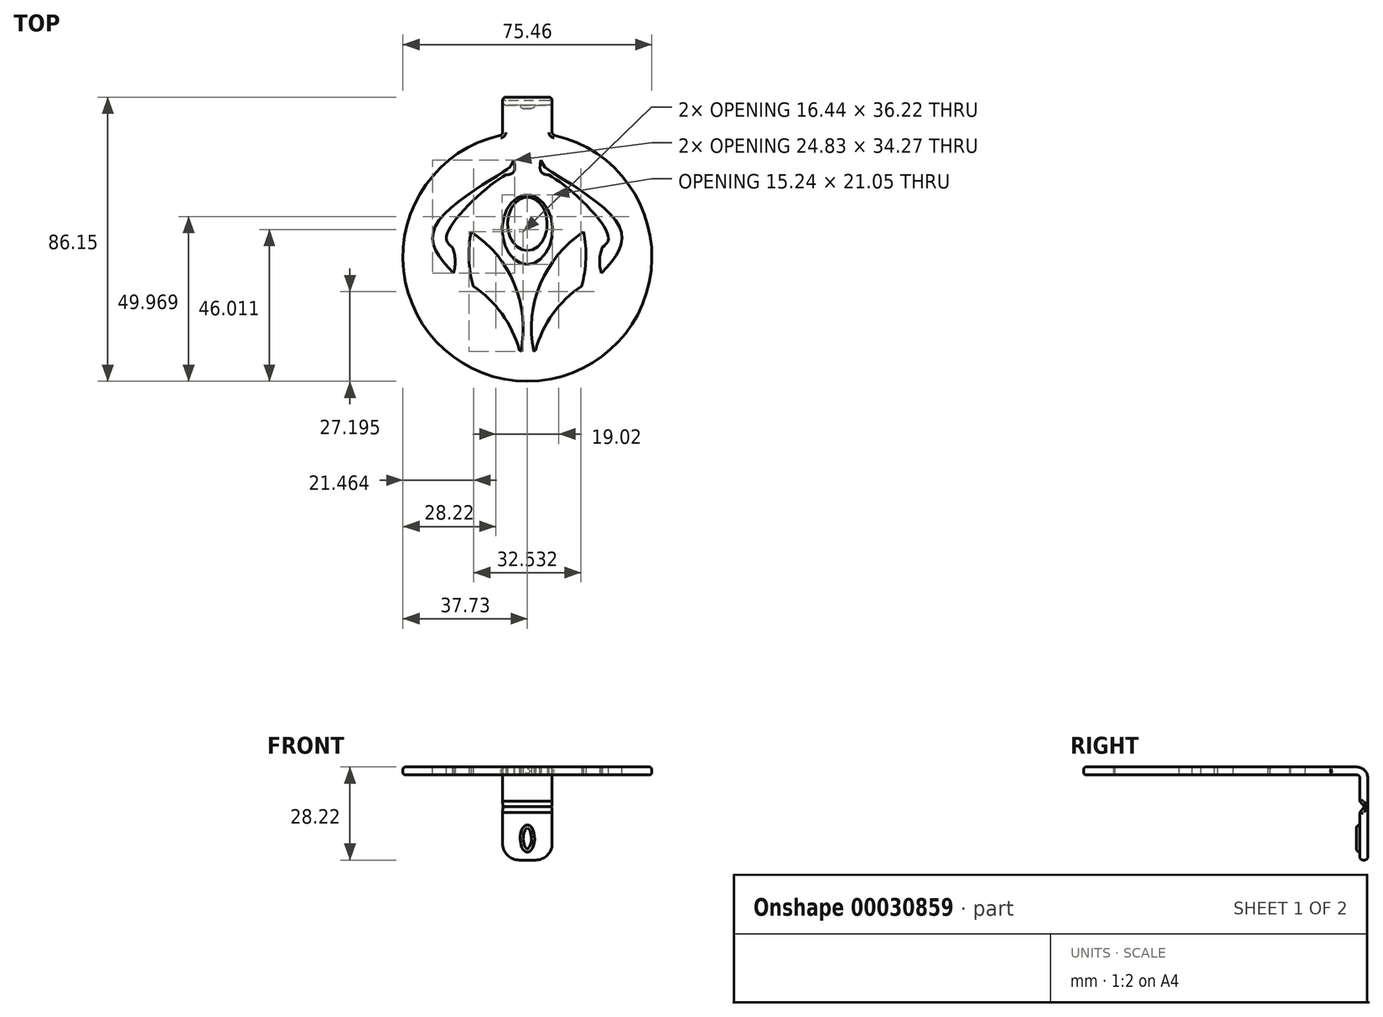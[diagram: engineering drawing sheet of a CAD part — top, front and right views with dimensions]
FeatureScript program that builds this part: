
annotation { "Feature Type Name" : "Feature", "Feature Type Description" : "" }
export const myFeature = defineFeature(function(context is Context, id is Id, definition is map)
    precondition{}
    {
        {
            var Q0;
            Q0=qCreatedBy(makeId("Top.planeOp"),FACE);
            var sketch = newSketch(context, id + "F0", { "sketchPlane" : qUnion([Q0])});
            skLineSegment(sketch, "E0", {"start": v(-75.5, -12.71) * mm, "end": v(-9.56, -74.3) * mm, "construction": true});
            skLineSegment(sketch, "E1", {"start": v(-4.86, -71.61) * mm, "end": v(-42.6, 18.94) * mm, "construction": true});
            skArc(sketch, "E2", {"start": v(-75.5, -12.71) * mm, "mid": v(-51.74, -53.37) * mm, "end": v(-9.56, -74.3) * mm});
            skArc(sketch, "E3", {"start": v(-4.86, -71.61) * mm, "mid": v(-9.83, -20.55) * mm, "end": v(-42.6, 18.94) * mm});
            skArc(sketch, "E4.MirrorCS", {"start": v(-75.5, -12.71) * mm, "mid": v(-33.32, -33.65) * mm, "end": v(-9.56, -74.3) * mm});
            skArc(sketch, "E5.0", {"start": v(-41.12, -22.06) * mm, "mid": v(-19.25, -43.28) * mm, "end": v(-6.12, -70.78) * mm});
            skArc(sketch, "E6.MirrorCS", {"start": v(-4.86, -71.61) * mm, "mid": v(-5.5, -71.2) * mm, "end": v(-6.12, -70.78) * mm});
            skArc(sketch, "E7.trimOffspring", {"start": v(-41.12, -22.06) * mm, "mid": v(-44.3, -1.65) * mm, "end": v(-42.6, 18.94) * mm});
            skArc(sketch, "E8.MirrorCS", {"start": v(75.5, -12.71) * mm, "mid": v(51.74, -53.37) * mm, "end": v(9.56, -74.3) * mm});
            skArc(sketch, "E9.MirrorCS", {"start": v(75.5, -12.71) * mm, "mid": v(33.32, -33.65) * mm, "end": v(9.56, -74.3) * mm});
            skArc(sketch, "E10.MirrorCS", {"start": v(41.12, -22.06) * mm, "mid": v(44.3, -1.65) * mm, "end": v(42.6, 18.94) * mm});
            skArc(sketch, "E11.MirrorCS", {"start": v(41.12, -22.06) * mm, "mid": v(19.25, -43.28) * mm, "end": v(6.12, -70.78) * mm});
            skArc(sketch, "E12.MirrorCS", {"start": v(4.86, -71.61) * mm, "mid": v(9.83, -20.55) * mm, "end": v(42.6, 18.94) * mm});
            skArc(sketch, "E13.MirrorCS", {"start": v(4.86, -71.61) * mm, "mid": v(5.5, -71.2) * mm, "end": v(6.12, -70.78) * mm});
            skSolve(sketch);
        }
        {
            var Q0;
            Q0=qCreatedBy(makeId("Top.planeOp"),FACE);
            var sketch = newSketch(context, id + "F1", { "sketchPlane" : qUnion([Q0])});
            skEllipse(sketch, "E14", {"center": v(0, 20.7) * mm, "majorRadius": 26.3 * mm, "minorRadius": 19.05 * mm, "majorAxis": v(0, -1)});
            skEllipse(sketch, "E15", {"center": v(0, 25) * mm, "majorRadius": 20.32 * mm, "minorRadius": 15 * mm, "majorAxis": v(0, -1)});
            skSolve(sketch);
        }
        {
            var Q0;
            Q0=qCreatedBy(makeId("Top.planeOp"),FACE);
            var sketch = newSketch(context, id + "F2", { "sketchPlane" : qUnion([Q0])});
            skFitSpline(sketch, "E16", {"points": [v(-10.32, 73.44) * mm, v(-14.62, 66.99) * mm, v(-69.19, 24.14) * mm, v(-56, -12.24) * mm], "startDerivative": vector(-33.58, -68.78) * mm, "endDerivative": vector(100.58, -102.34) * mm});
            skArc(sketch, "E17", {"start": v(-56, -12.24) * mm, "mid": v(-54.75, -2.43) * mm, "end": v(-56.87, 7.24) * mm});
            skFitSpline(sketch, "E18", {"points": [v(-56.87, 7.24) * mm, v(-60.9, 17.24) * mm, v(-16.13, 62.2) * mm], "startDerivative": vector(-32.39, 22.42) * mm, "endDerivative": vector(56.1, 28.88) * mm});
            skFitSpline(sketch, "E19", {"points": [v(-10.32, 73.44) * mm, v(-10.32, 64.63) * mm, v(-16.13, 62.2) * mm], "startDerivative": vector(3.32, -19.88) * mm, "endDerivative": vector(-13.95, 1.21) * mm});
            skFitSpline(sketch, "E20.MirrorCS", {"points": [v(10.32, 73.44) * mm, v(10.32, 64.63) * mm, v(16.13, 62.2) * mm], "startDerivative": vector(-3.32, -19.88) * mm, "endDerivative": vector(13.95, 1.21) * mm});
            skFitSpline(sketch, "E21.MirrorCS", {"points": [v(10.32, 73.44) * mm, v(14.62, 66.99) * mm, v(69.19, 24.14) * mm, v(56, -12.24) * mm], "startDerivative": vector(33.58, -68.78) * mm, "endDerivative": vector(-100.58, -102.34) * mm});
            skFitSpline(sketch, "E22.MirrorCS", {"points": [v(56.87, 7.24) * mm, v(60.9, 17.24) * mm, v(16.13, 62.2) * mm], "startDerivative": vector(32.39, 22.42) * mm, "endDerivative": vector(-56.1, 28.88) * mm});
            skArc(sketch, "E23.MirrorCS", {"start": v(56, -12.24) * mm, "mid": v(54.75, -2.43) * mm, "end": v(56.87, 7.24) * mm});
            skSolve(sketch);
        }
        {
            var Q0;
            Q0=qCreatedBy(makeId("Top.planeOp"),FACE);
            var sketch = newSketch(context, id + "F3", { "sketchPlane" : qUnion([Q0])});
            skCircle(sketch, "E24", {"center": v(0, 0) * mm, "radius": 94.33 * mm});
            skSolve(sketch);
        }
        {
            var Q0;
            Q0=makeQuery(id+"F3.imprint","IMPRINT",FACE,{"disambiguationData":[TD([[makeQuery(id+"F3.imprint","IMPRINT",EDGE,{"derivedFrom":sQuery(id+"F3.wireOp",EDGE,"E24")}),1.0]])]});
            extrude(context, id + "F4", {"entities" : qUnion([Q0]), "endBound" : BoundingType.SYMMETRIC, "depth" : 6 * mm});
        }
        {
            var Q0;
            Q0=makeQuery(id+"F0.imprint","IMPRINT",FACE,{"disambiguationData":[TD([[makeQuery(id+"F0.imprint","IMPRINT",EDGE,{"derivedFrom":sQuery(id+"F0.wireOp",EDGE,"E8.MirrorCS")}),-1.0]])]});
            var Q1;
            Q1=makeQuery(id+"F0.imprint","IMPRINT",FACE,{"disambiguationData":[TD([[makeQuery(id+"F0.imprint","IMPRINT",EDGE,{"derivedFrom":sQuery(id+"F0.wireOp",EDGE,"E10.MirrorCS")}),1.0]])]});
            var Q2;
            Q2=makeQuery(id+"F0.imprint","IMPRINT",FACE,{"disambiguationData":[TD([[makeQuery(id+"F0.imprint","IMPRINT",EDGE,{"derivedFrom":sQuery(id+"F0.wireOp",EDGE,"E3")}),1.0]])]});
            var Q3;
            Q3=makeQuery(id+"F0.imprint","IMPRINT",FACE,{"disambiguationData":[TD([[makeQuery(id+"F0.imprint","IMPRINT",EDGE,{"derivedFrom":sQuery(id+"F0.wireOp",EDGE,"E4.MirrorCS")}),-1.0]])]});
            var Q4;
            Q4=makeQuery(id+"F2.imprint","IMPRINT",FACE,{"disambiguationData":[TD([[makeQuery(id+"F2.imprint","IMPRINT",EDGE,{"derivedFrom":sQuery(id+"F2.wireOp",EDGE,"E16")}),1.0]])]});
            var Q5;
            Q5=makeQuery(id+"F2.imprint","IMPRINT",FACE,{"disambiguationData":[TD([[makeQuery(id+"F2.imprint","IMPRINT",EDGE,{"derivedFrom":sQuery(id+"F2.wireOp",EDGE,"E20.MirrorCS")}),1.0]])]});
            var Q6;
            Q6=makeQuery(id+"F1.imprint","IMPRINT",FACE,{"disambiguationData":[TD([[makeQuery(id+"F1.imprint","IMPRINT",EDGE,{"derivedFrom":sQuery(id+"F1.wireOp",EDGE,"E14")}),1.0]])]});
            extrude(context, id + "F5", {"entities" : qUnion([Q0, Q1, Q2, Q3, Q4, Q5, Q6]), "operationType" : NewBodyOperationType.REMOVE, "endBound" : BoundingType.SYMMETRIC, "depth" : 25 * mm});
        }
        {
            var Q0;
            Q0=qCreatedBy(makeId("Front.planeOp"),FACE);
            cPlane(context, id + "F6", {"entities" : qUnion([Q0]), "cplaneType" : CPlaneType.OFFSET, "offset" : 50 * mm, "oppositeDirection" : true, "width" : 150 * mm, "height" : 150 * mm});
        }
        {
            var Q0;
            Q0=qCreatedBy(id+"F6.planeOp",FACE);
            var sketch = newSketch(context, id + "F7", { "sketchPlane" : qUnion([Q0])});
            skCircle(sketch, "E25", {"center": v(0, 0) * mm, "radius": 1.81 * mm});
            skSolve(sketch);
        }
        {
            var Q0;
            Q0=qSketchRegion(id+"F7",true);
            var Q1;
            Q1=makeQuery(id+"F5.boolean.opBoolean","COPY",FACE,{"derivedFrom":makeQuery(id+"F5.opExtrude","SWEPT_FACE",FACE,{"disambiguationData":[OSD([sQuery(id+"F1.wireOp",EDGE,"E15")])]})});
            extrude(context, id + "F8", {"entities" : qUnion([Q0]), "operationType" : NewBodyOperationType.ADD, "endBound" : BoundingType.UP_TO_SURFACE, "endBoundEntityFace" : qUnion([Q1]), "depth" : 25 * mm});
        }
        {
            var Q0;
            Q0=makeQuery(id+"F4.opExtrude","CAP_EDGE",EDGE,{"disambiguationData":[OSD([sQuery(id+"F3.wireOp",EDGE,"E24")])],"isStart":false});
            var Q1;
            Q1=makeQuery(id+"F4.opExtrude","CAP_EDGE",EDGE,{"disambiguationData":[OSD([sQuery(id+"F3.wireOp",EDGE,"E24")])],"isStart":true});
            fillet(context, id + "F9", {"entities" : qUnion([Q0, Q1]), "radius" : 2 * mm, "tangentPropagation" : true, "allowEdgeOverflow" : false});
        }
        {
            var Q0;
            Q0=makeQuery(id+"F5.boolean.opBoolean","SPLIT",BODY,{"disambiguationData":[OD(0.0)],"derivedFrom":makeQuery(id+"F4.opExtrude","SWEPT_BODY",BODY,{"disambiguationData":[OSD([sQuery(id+"F3.wireOp",EDGE,"E24")])]})});
            var Q1;
            Q1=qCreatedBy(makeId("Origin.pointOp"),VERTEX);
            transform(context, id + "F10", {"entities" : qUnion([Q0]), "transformType" : TransformType.SCALE_UNIFORMLY, "scale" : 0.4, "makeCopy" : false, "scalePoint" : qUnion([Q1])});
        }
        {
            var Q0;
            Q0=qCreatedBy(makeId("Front.planeOp"),FACE);
            cPlane(context, id + "F11", {"entities" : qUnion([Q0]), "cplaneType" : CPlaneType.OFFSET, "offset" : 35 * mm, "oppositeDirection" : true, "width" : 150 * mm, "height" : 150 * mm});
        }
        {
            var Q0;
            Q0=qCreatedBy(id+"F11.planeOp",FACE);
            var sketch = newSketch(context, id + "F12", { "sketchPlane" : qUnion([Q0])});
            skLineSegment(sketch, "E26.rect.bottom", {"start": v(-7.5, 1.2) * mm, "end": v(7.5, 1.2) * mm});
            skLineSegment(sketch, "E26.rect.top", {"start": v(-7.5, -1.2) * mm, "end": v(7.5, -1.2) * mm});
            skLineSegment(sketch, "E26.rect.left", {"start": v(-7.5, 1.2) * mm, "end": v(-7.5, -1.2) * mm});
            skLineSegment(sketch, "E26.rect.right", {"start": v(7.5, 1.2) * mm, "end": v(7.5, -1.2) * mm});
            skPoint(sketch, "E26.rect.middle", {"position": v(0, 0) * mm});
            skLineSegment(sketch, "E27.0", {"start": v(-36.93, 1.2) * mm, "end": v(36.93, 1.2) * mm, "construction": true});
            skLineSegment(sketch, "E28.1", {"start": v(36.93, -1.2) * mm, "end": v(-36.93, -1.2) * mm, "construction": true});
            skPoint(sketch, "E29", {"position": v(0, 1.2) * mm});
            skPoint(sketch, "E30", {"position": v(0, -1.2) * mm});
            skSolve(sketch);
        }
        {
            var Q0;
            Q0=qCreatedBy(makeId("Right.planeOp"),FACE);
            var sketch = newSketch(context, id + "F13", { "sketchPlane" : qUnion([Q0])});
            skPoint(sketch, "E31.0", {"position": v(35, 1.2) * mm});
            skLineSegment(sketch, "E32", {"start": v(35, 1.2) * mm, "end": v(45.12, 1.2) * mm});
            skArc(sketch, "E33", {"start": v(48.42, -2.1) * mm, "mid": v(47.46, 0.23) * mm, "end": v(45.12, 1.2) * mm});
            skLineSegment(sketch, "E34", {"start": v(48.42, -2.1) * mm, "end": v(48.42, -27.02) * mm});
            skSolve(sketch);
        }
        {
            var Q0;
            Q0=makeQuery(id+"F12.imprint","IMPRINT",FACE,{"disambiguationData":[TD([[makeQuery(id+"F12.imprint","IMPRINT",EDGE,{"derivedFrom":sQuery(id+"F12.wireOp",EDGE,"E26.rect.bottom")}),-1.0]])]});
            var Q1;
            Q1 = qConstructionFilter(qBodyType(qCreatedBy(id + "F13" ,EDGE), BodyType.WIRE), ConstructionObject.NO);
            sweep(context, id + "F14", {"operationType" : NewBodyOperationType.ADD, "profiles" : qUnion([Q0]), "path" : qUnion([Q1])});
        }
        {
            var Q0;
            Q0=makeQuery(id+"F14.opSweep","SWEPT_FACE",FACE,{"disambiguationData":[OSD([sQuery(id+"F12.wireOp",EDGE,"E26.rect.left"),sQuery(id+"F13.wireOp",EDGE,"E32")])]});
            var sketch = newSketch(context, id + "F15", { "sketchPlane" : qUnion([Q0])});
            skLineSegment(sketch, "E35", {"start": v(-46.02, -9.2) * mm, "end": v(-47.42, -10.87) * mm});
            skLineSegment(sketch, "E36", {"start": v(-47.42, -10.87) * mm, "end": v(-46.02, -12.54) * mm});
            skLineSegment(sketch, "E37", {"start": v(-46.02, -12.54) * mm, "end": v(-46.02, -9.2) * mm});
            skPoint(sketch, "E38", {"position": v(-46.02, -10.87) * mm});
            skSolve(sketch);
        }
        {
            var Q0;
            Q0=makeQuery(id+"F15.imprint","IMPRINT",FACE,{"disambiguationData":[TD([[makeQuery(id+"F15.imprint","IMPRINT",EDGE,{"derivedFrom":sQuery(id+"F15.wireOp",EDGE,"E35")}),1.0]])]});
            extrude(context, id + "F16", {"entities" : qUnion([Q0]), "operationType" : NewBodyOperationType.REMOVE, "endBound" : BoundingType.UP_TO_NEXT, "oppositeDirection" : true, "depth" : 25 * mm});
        }
        {
            var Q0;
            Q0=makeQuery(id+"F14.opSweep","CAP_EDGE",EDGE,{"disambiguationData":[OSD([sQuery(id+"F12.wireOp",EDGE,"E26.rect.right"),sQuery(id+"F13.wireOp",VERTEX,"E34.end")])],"isStart":false});
            var Q1;
            Q1=makeQuery(id+"F14.opSweep","CAP_EDGE",EDGE,{"disambiguationData":[OSD([sQuery(id+"F12.wireOp",EDGE,"E26.rect.left"),sQuery(id+"F13.wireOp",VERTEX,"E34.end")])],"isStart":false});
            fillet(context, id + "F17", {"entities" : qUnion([Q0, Q1]), "radius" : 5 * mm, "tangentPropagation" : true, "allowEdgeOverflow" : false});
        }
        {
            var Q0;
            Q0=makeQuery(id+"F14.opSweep","CAP_FACE",FACE,{"disambiguationData":[OSD([sQuery(id+"F12.wireOp",EDGE,"E26.rect.bottom"),sQuery(id+"F12.wireOp",EDGE,"E26.rect.top"),sQuery(id+"F12.wireOp",EDGE,"E26.rect.left"),sQuery(id+"F12.wireOp",EDGE,"E26.rect.right"),sQuery(id+"F13.wireOp",VERTEX,"E34.end")])],"isStart":false});
            var Q1;
            Q1=makeQuery(id+"F14.opSweep","SWEPT_FACE",FACE,{"disambiguationData":[OSD([sQuery(id+"F12.wireOp",EDGE,"E26.rect.left"),sQuery(id+"F13.wireOp",EDGE,"E32")])]});
            var Q2;
            Q2=makeQuery(id+"F14.opSweep","SWEPT_FACE",FACE,{"disambiguationData":[OSD([sQuery(id+"F12.wireOp",EDGE,"E26.rect.right"),sQuery(id+"F13.wireOp",EDGE,"E32")])]});
            fillet(context, id + "F18", {"entities" : qUnion([Q0, Q1, Q2]), "radius" : 1 * mm, "tangentPropagation" : true, "allowEdgeOverflow" : false});
        }
        {
            var Q0;
            {var subQ0=sQuery(id+"F12.wireOp",EDGE,"E26.rect.top");Q0=makeQuery(id+"F16.boolean.opBoolean","SPLIT",FACE,{"disambiguationData":[TD([makeQuery(id+"F16.opExtrude","SWEPT_FACE",FACE,{"disambiguationData":[OSD([sQuery(id+"F15.wireOp",EDGE,"E36")])]})])],"derivedFrom":makeQuery(id+"F14.opSweep","SWEPT_FACE",FACE,{"disambiguationData":[OSD([subQ0,sQuery(id+"F13.wireOp",EDGE,"E34")])]})});}
            var sketch = newSketch(context, id + "F19", { "sketchPlane" : qUnion([Q0])});
            skEllipse(sketch, "E39", {"center": v(0, -20.48) * mm, "majorRadius": 4.13 * mm, "minorRadius": 2.2 * mm, "majorAxis": v(0, 1)});
            skSolve(sketch);
        }
        {
            var Q0;
            Q0 = qSketchRegion(id + "F19", true);
            extrude(context, id + "F20", {"entities" : qUnion([Q0]), "operationType" : NewBodyOperationType.ADD, "depth" : 1 * mm});
        }
        {
            var Q0;
            Q0=makeQuery(id+"F20.opExtrude","CAP_FACE",FACE,{"disambiguationData":[OSD([sQuery(id+"F19.wireOp",EDGE,"E39")])],"isStart":false});
            fillet(context, id + "F21", {"entities" : qUnion([Q0]), "radius" : 0.95 * mm, "tangentPropagation" : true, "allowEdgeOverflow" : false});
        }
    });
